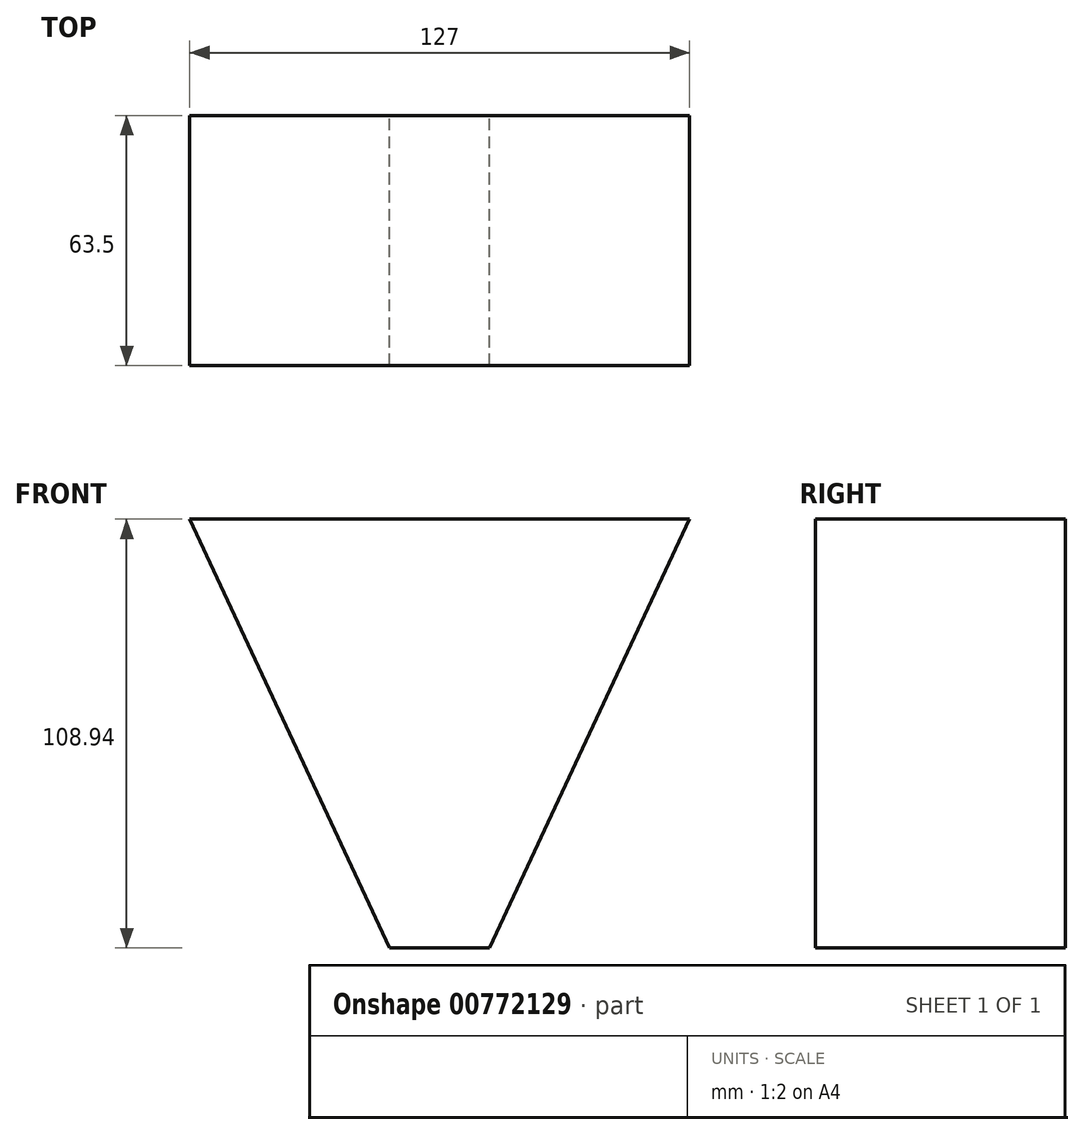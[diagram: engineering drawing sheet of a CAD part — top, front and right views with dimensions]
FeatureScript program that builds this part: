
annotation { "Feature Type Name" : "Feature", "Feature Type Description" : "" }
export const myFeature = defineFeature(function(context is Context, id is Id, definition is map)
    precondition{}
    {
        {
            var Q0;
            Q0=qCreatedBy(makeId("Front.planeOp"),FACE);
            var sketch = newSketch(context, id + "F0", { "sketchPlane" : qUnion([Q0])});
            skLineSegment(sketch, "E0", {"start": v(61.85, 0) * mm, "end": v(-65.15, 0) * mm});
            skLineSegment(sketch, "E1", {"start": v(-65.15, 0) * mm, "end": v(-14.35, -108.94) * mm});
            skLineSegment(sketch, "E2", {"start": v(-14.35, -108.94) * mm, "end": v(11.05, -108.94) * mm});
            skLineSegment(sketch, "E3", {"start": v(11.05, -108.94) * mm, "end": v(61.85, 0) * mm});
            skSolve(sketch);
        }
        {
            var Q0;
            Q0=makeQuery(id+"F0.imprint","IMPRINT",FACE,{"disambiguationData":[TD([[makeQuery(id+"F0.imprint","IMPRINT",EDGE,{"derivedFrom":sQuery(id+"F0.wireOp",EDGE,"E0")}),1.0]])]});
            extrude(context, id + "F1", {"entities" : qUnion([Q0]), "endBound" : BoundingType.SYMMETRIC, "depth" : 63.5 * mm, "offsetDistance" : 25.4 * mm});
        }
    });
